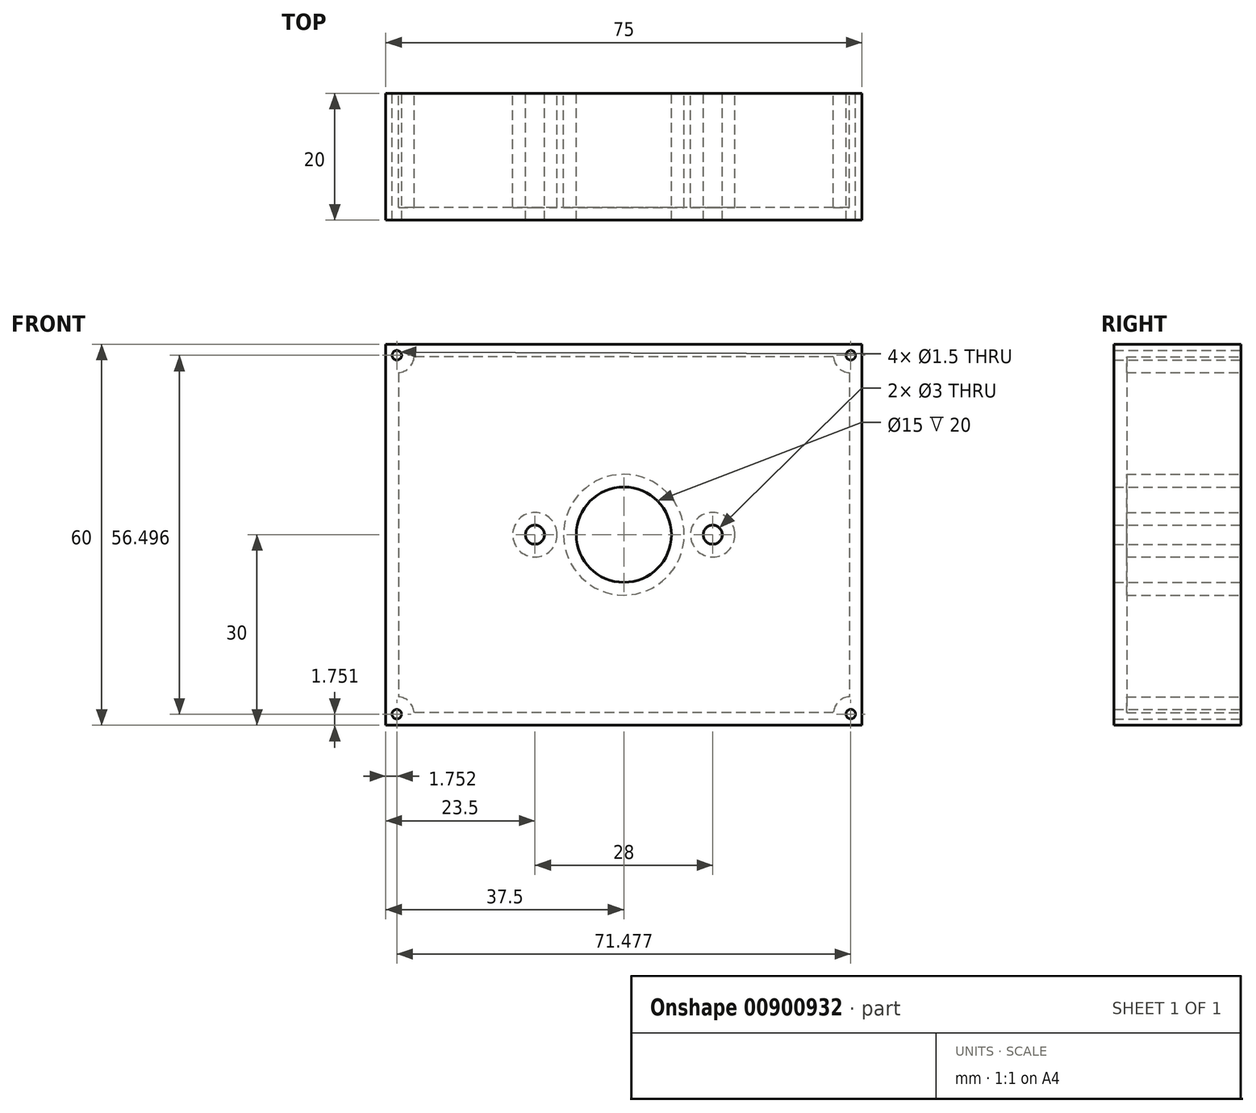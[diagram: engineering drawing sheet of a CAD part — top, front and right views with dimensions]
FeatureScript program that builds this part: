
annotation { "Feature Type Name" : "Feature", "Feature Type Description" : "" }
export const myFeature = defineFeature(function(context is Context, id is Id, definition is map)
    precondition{}
    {
        {
            var Q0;
            Q0=qCreatedBy(makeId("Front.planeOp"),FACE);
            var sketch = newSketch(context, id + "F0", { "sketchPlane" : qUnion([Q0])});
            skLineSegment(sketch, "E0.bottom", {"start": v(37.5, 30) * mm, "end": v(-37.5, 30) * mm});
            skLineSegment(sketch, "E0.top", {"start": v(37.5, -30) * mm, "end": v(-37.5, -30) * mm});
            skLineSegment(sketch, "E0.left", {"start": v(37.5, 30) * mm, "end": v(37.5, -30) * mm});
            skLineSegment(sketch, "E0.right", {"start": v(-37.5, 30) * mm, "end": v(-37.5, -30) * mm});
            skPoint(sketch, "E0.middle", {"position": v(0, 0) * mm});
            skCircle(sketch, "E1", {"center": v(0, 0) * mm, "radius": 7.5 * mm});
            skCircle(sketch, "E2", {"center": v(14, 0) * mm, "radius": 1.5 * mm});
            skCircle(sketch, "E3", {"center": v(-14, 0) * mm, "radius": 1.5 * mm});
            skLineSegment(sketch, "E4.bottom", {"start": v(-37.5, 30) * mm, "end": v(-36.5, 30) * mm});
            skLineSegment(sketch, "E4.top", {"start": v(-37.5, -29.02) * mm, "end": v(-36.5, -29.02) * mm});
            skLineSegment(sketch, "E4.left", {"start": v(-37.5, 30) * mm, "end": v(-37.5, -29.02) * mm});
            skLineSegment(sketch, "E5.bottom", {"start": v(-36.5, 30) * mm, "end": v(37.5, 30) * mm});
            skLineSegment(sketch, "E5.left", {"start": v(-36.5, 30) * mm, "end": v(-36.5, 29) * mm});
            skLineSegment(sketch, "E5.right", {"start": v(37.5, 30) * mm, "end": v(37.5, 29) * mm});
            skCircle(sketch, "E6", {"center": v(-35.74, 28.25) * mm, "radius": 0.75 * mm});
            skCircle(sketch, "E7", {"center": v(35.73, 28.24) * mm, "radius": 0.75 * mm});
            skLineSegment(sketch, "E8.bottom", {"start": v(-37.5, -30) * mm, "end": v(37.49, -30) * mm});
            skLineSegment(sketch, "E8.left", {"start": v(-37.5, -30) * mm, "end": v(-37.5, -29) * mm});
            skLineSegment(sketch, "E8.right", {"start": v(37.49, -30) * mm, "end": v(37.49, -29) * mm});
            skLineSegment(sketch, "E9.bottom", {"start": v(37.49, -29) * mm, "end": v(36.49, -29) * mm});
            skLineSegment(sketch, "E9.top", {"start": v(37.49, 28.96) * mm, "end": v(36.49, 28.96) * mm});
            skLineSegment(sketch, "E9.left", {"start": v(37.49, -29) * mm, "end": v(37.49, 28.96) * mm});
            skCircle(sketch, "E10", {"center": v(35.73, -28.24) * mm, "radius": 0.75 * mm});
            skCircle(sketch, "E11", {"center": v(-35.75, -28.25) * mm, "radius": 0.75 * mm});
            skSolve(sketch);
        }
        {
            var Q0;
            Q0 = qSketchRegion(id + "F0", true);
            extrude(context, id + "F1", {"entities" : qUnion([Q0]), "endBound" : BoundingType.SYMMETRIC, "depth" : 20 * mm, "offsetDistance" : 25.4 * mm});
        }
        {
            var Q0;
            Q0=makeQuery(id+"F1.opExtrude","CAP_FACE",FACE,{"disambiguationData":[OSD([sQuery(id+"F0.wireOp",EDGE,"E0.top"),sQuery(id+"F0.wireOp",EDGE,"E0.left"),sQuery(id+"F0.wireOp",EDGE,"E1"),sQuery(id+"F0.wireOp",EDGE,"E2"),sQuery(id+"F0.wireOp",EDGE,"E3"),sQuery(id+"F0.wireOp",EDGE,"E4.bottom"),sQuery(id+"F0.wireOp",EDGE,"E4.left"),sQuery(id+"F0.wireOp",EDGE,"E5.bottom"),sQuery(id+"F0.wireOp",EDGE,"E5.right"),sQuery(id+"F0.wireOp",EDGE,"E6"),sQuery(id+"F0.wireOp",EDGE,"E7"),sQuery(id+"F0.wireOp",EDGE,"E8.bottom"),sQuery(id+"F0.wireOp",EDGE,"E8.left"),sQuery(id+"F0.wireOp",EDGE,"E10"),sQuery(id+"F0.wireOp",EDGE,"E11")])],"isStart":true});
            shell(context, id + "F2", {"entities" : qUnion([Q0]), "thickness" : 2 * mm});
        }
    });
